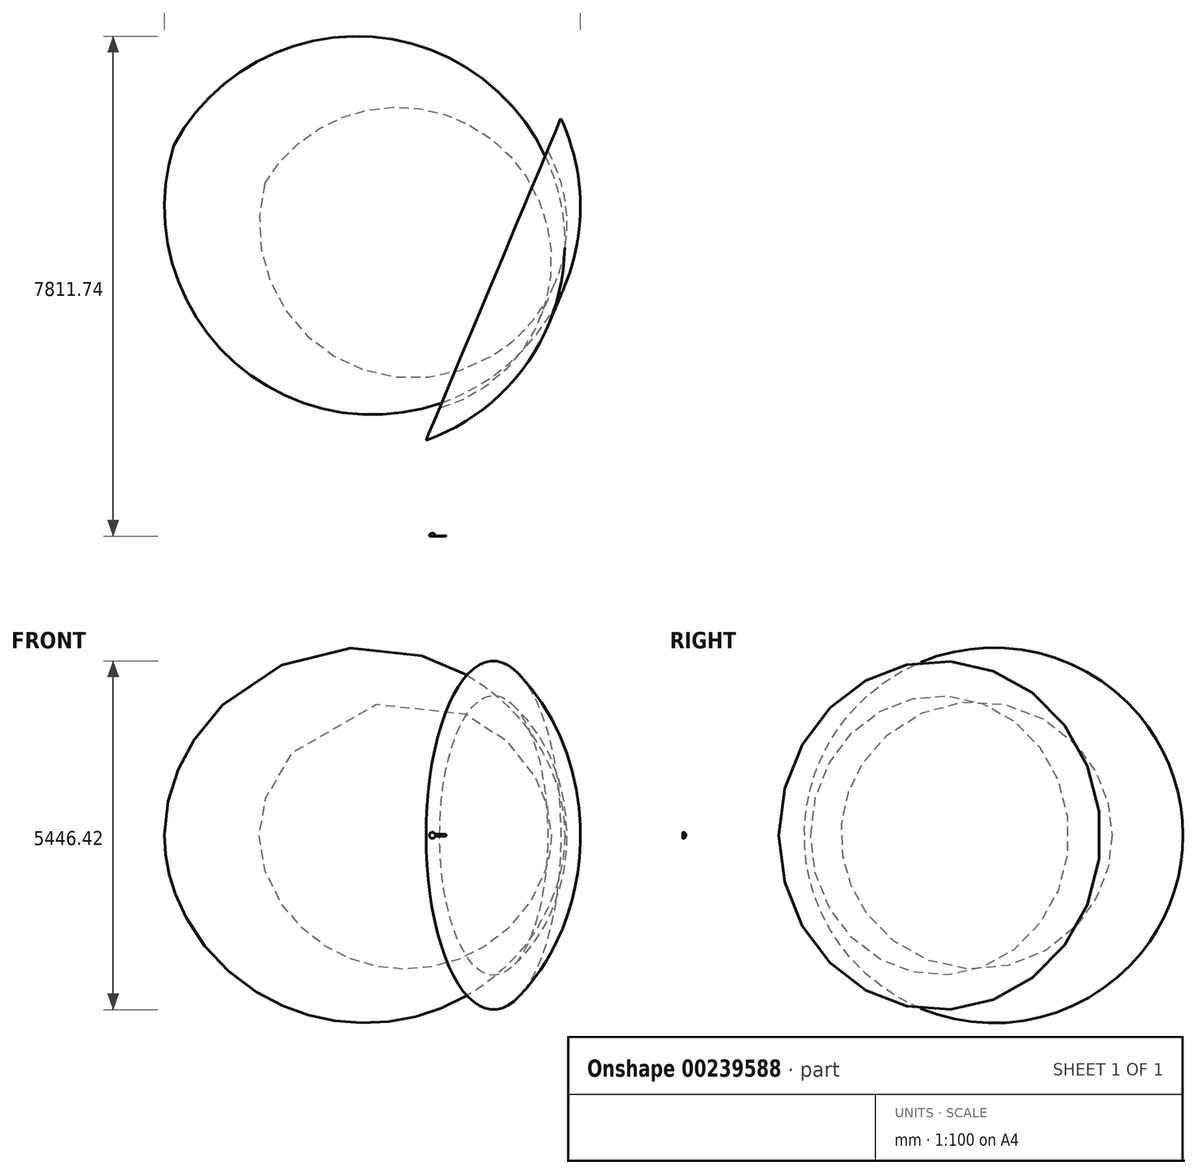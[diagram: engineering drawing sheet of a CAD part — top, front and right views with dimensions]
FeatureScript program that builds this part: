
annotation { "Feature Type Name" : "Feature", "Feature Type Description" : "" }
export const myFeature = defineFeature(function(context is Context, id is Id, definition is map)
    precondition{}
    {
        {
            var Q0;
            Q0=qCreatedBy(makeId("Top.planeOp"),FACE);
            var sketch = newSketch(context, id + "F0", { "sketchPlane" : qUnion([Q0])});
            skArc(sketch, "E0", {"start": v(1771.28, 3621.52) * mm, "mid": v(2095.1, 4794.88) * mm, "end": v(1801.55, 5976.18) * mm});
            skArc(sketch, "E1", {"start": v(1923.07, 3557.94) * mm, "mid": v(2310.56, 5007.05) * mm, "end": v(2005.7, 6475.78) * mm});
            skLineSegment(sketch, "E2", {"start": v(1771.28, 3621.52) * mm, "end": v(1923.07, 3557.94) * mm});
            skLineSegment(sketch, "E3", {"start": v(1801.55, 5976.18) * mm, "end": v(2005.7, 6475.78) * mm});
            skLineSegment(sketch, "E4", {"start": v(-511.66, 4577.77) * mm, "end": v(3489.42, 2901.85) * mm, "construction": true});
            skSolve(sketch);
        }
        {
            var Q0;
            Q0=makeQuery(id+"F0.imprint","IMPRINT",FACE,{"disambiguationData":[TD([[makeQuery(id+"F0.imprint","IMPRINT",EDGE,{"derivedFrom":sQuery(id+"F0.wireOp",EDGE,"E0")}),-1.0]])]});
            var Q1;
            Q1=sQuery(id+"F0.wireOp",EDGE,"E4");
            revolve(context, id + "F1", {"entities" : qUnion([Q0]), "axis" : qUnion([Q1]), "revolveType" : RevolveType.FULL});
        }
        {
            var Q0;
            Q0=qCreatedBy(makeId("Top.planeOp"),FACE);
            var sketch = newSketch(context, id + "F2", { "sketchPlane" : qUnion([Q0])});
            skArc(sketch, "E5", {"start": v(0, 0) * mm, "mid": v(-33.92, -14.05) * mm, "end": v(-47.98, -47.98) * mm});
            skArc(sketch, "E6", {"start": v(0, 0.26) * mm, "mid": v(-34.1, -13.87) * mm, "end": v(-48.23, -47.98) * mm});
            skLineSegment(sketch, "E7", {"start": v(-47.98, -47.98) * mm, "end": v(-48.23, -47.98) * mm});
            skLineSegment(sketch, "E8", {"start": v(0, 0) * mm, "end": v(0, 0.26) * mm});
            skLineSegment(sketch, "E9", {"start": v(0, 42.8) * mm, "end": v(0, -101.5) * mm, "construction": true});
            skSolve(sketch);
        }
        {
            var Q0;
            Q0=makeQuery(id+"F2.imprint","IMPRINT",FACE,{"disambiguationData":[TD([[makeQuery(id+"F2.imprint","IMPRINT",EDGE,{"derivedFrom":sQuery(id+"F2.wireOp",EDGE,"E5")}),-1.0]])]});
            var Q1;
            Q1=sQuery(id+"F2.wireOp",EDGE,"E9");
            revolve(context, id + "F3", {"entities" : qUnion([Q0]), "axis" : qUnion([Q1]), "revolveType" : RevolveType.FULL});
        }
        {
            var Q0;
            Q0=makeQuery(id+"F3.opRevolve","SWEPT_FACE",FACE,{"disambiguationData":[OSD([sQuery(id+"F2.wireOp",EDGE,"E7")])]});
            var sketch = newSketch(context, id + "F4", { "sketchPlane" : qUnion([Q0])});
            skLineSegment(sketch, "E10", {"start": v(45.55, 15.88) * mm, "end": v(201.12, 15.88) * mm});
            skLineSegment(sketch, "E11", {"start": v(48.23, 0) * mm, "end": v(49.86, 0) * mm, "construction": true});
            skLineSegment(sketch, "E12", {"start": v(49.86, 0) * mm, "end": v(49.86, 0) * mm, "construction": true});
            skArc(sketch, "E13", {"start": v(201.12, 15.88) * mm, "mid": v(212.35, 11.23) * mm, "end": v(217, 0) * mm});
            skLineSegment(sketch, "E14.MirrorCS", {"start": v(45.55, -15.88) * mm, "end": v(201.12, -15.88) * mm});
            skArc(sketch, "E15.MirrorCS", {"start": v(201.12, -15.87) * mm, "mid": v(212.35, -11.23) * mm, "end": v(217, 0) * mm});
            skSolve(sketch);
        }
        {
            var Q0;
            Q0 = qSketchRegion(id + "F4", true);
            var Q1;
            {var subQ1=sQuery(id+"F4.wireOp",EDGE,"E10");Q1=makeQuery(id+"F4.imprint","IMPRINT",FACE,{"disambiguationData":[TD([[makeQuery(id+"F4.imprint","IMPRINT",EDGE,{"derivedFrom":subQ1}),-1.0]])]});}
            extrude(context, id + "F5", {"entities" : qUnion([Q0, Q1]), "oppositeDirection" : true, "depth" : 5.08 * mm});
        }
    });
